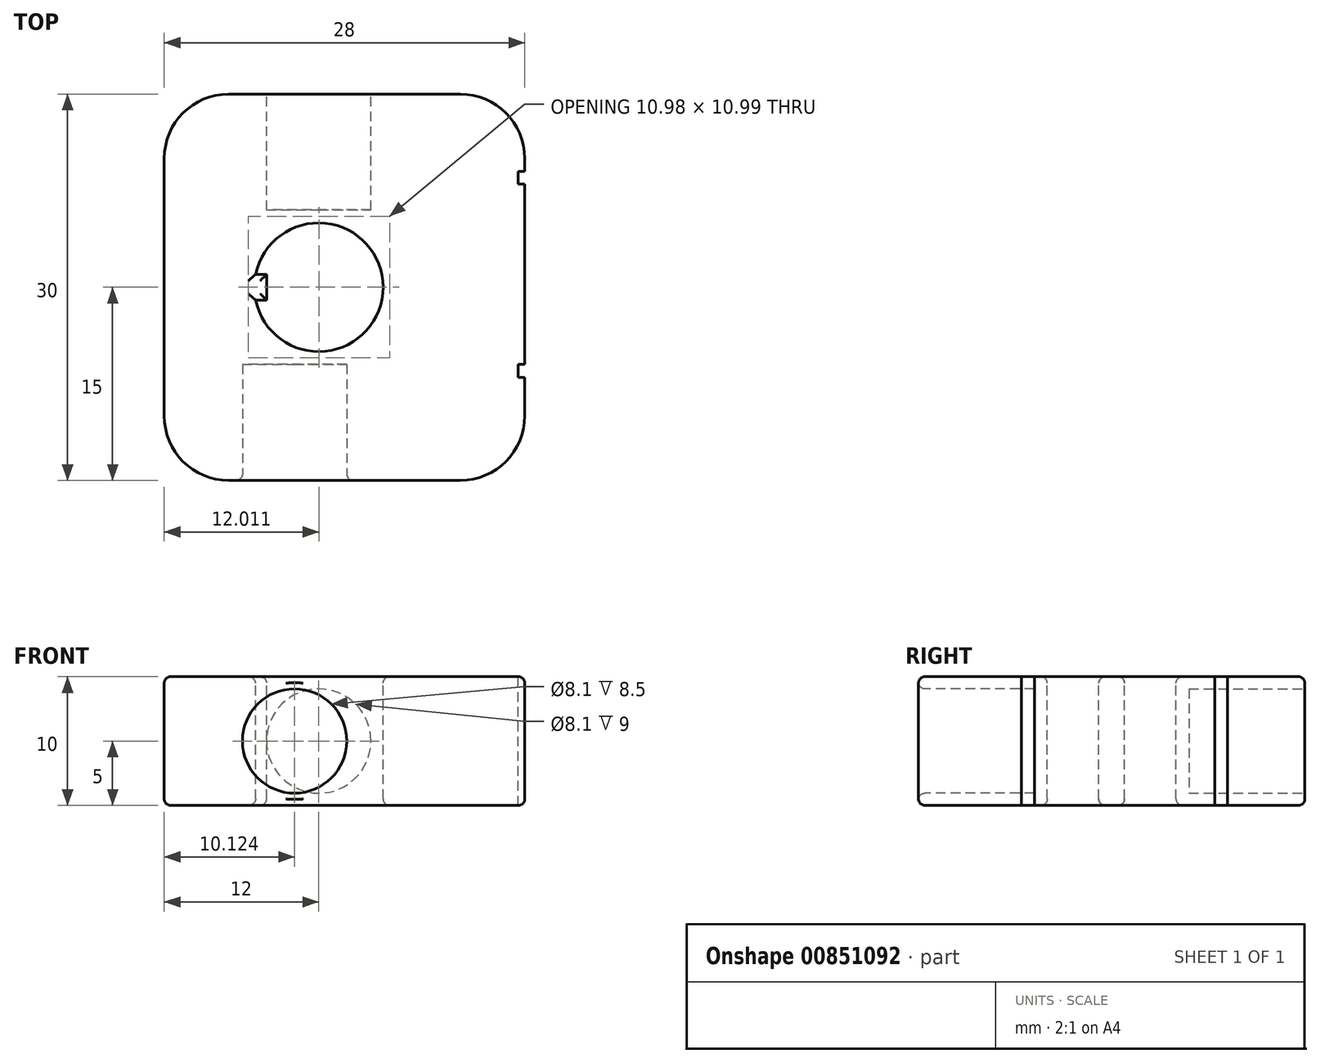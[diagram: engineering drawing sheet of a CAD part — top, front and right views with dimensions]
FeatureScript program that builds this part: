
annotation { "Feature Type Name" : "Feature", "Feature Type Description" : "" }
export const myFeature = defineFeature(function(context is Context, id is Id, definition is map)
    precondition{}
    {
        {
            var Q0;
            Q0=qCreatedBy(makeId("Top.planeOp"),FACE);
            var sketch = newSketch(context, id + "F0", { "sketchPlane" : qUnion([Q0])});
            skLineSegment(sketch, "E0.bottom", {"start": v(9, -15) * mm, "end": v(-9, -15) * mm});
            skLineSegment(sketch, "E0.top", {"start": v(9, 15) * mm, "end": v(-9, 15) * mm});
            skLineSegment(sketch, "E0.left", {"start": v(14, -10) * mm, "end": v(14, 10) * mm});
            skLineSegment(sketch, "E0.right", {"start": v(-14, -10) * mm, "end": v(-14, 10) * mm});
            skPoint(sketch, "E0.middle", {"position": v(0, 0) * mm});
            skPoint(sketch, "E1.visualSharp", {"position": v(-14, -15) * mm});
            skArc(sketch, "E1.filletArc", {"start": v(-14, -10) * mm, "mid": v(-12.54, -13.54) * mm, "end": v(-9, -15) * mm});
            skPoint(sketch, "E2.visualSharp", {"position": v(-14, 15) * mm});
            skArc(sketch, "E2.filletArc", {"start": v(-9, 15) * mm, "mid": v(-12.54, 13.54) * mm, "end": v(-14, 10) * mm});
            skPoint(sketch, "E3.visualSharp", {"position": v(14, 15) * mm});
            skArc(sketch, "E3.filletArc", {"start": v(14, 10) * mm, "mid": v(12.54, 13.54) * mm, "end": v(9, 15) * mm});
            skPoint(sketch, "E4.visualSharp", {"position": v(14, -15) * mm});
            skArc(sketch, "E4.filletArc", {"start": v(9, -15) * mm, "mid": v(12.54, -13.54) * mm, "end": v(14, -10) * mm});
            skSolve(sketch);
        }
        {
            var Q0;
            Q0=makeQuery(id+"F0.imprint","IMPRINT",FACE,{"disambiguationData":[TD([[makeQuery(id+"F0.imprint","IMPRINT",EDGE,{"derivedFrom":sQuery(id+"F0.wireOp",EDGE,"E0.bottom")}),-1.0]])]});
            extrude(context, id + "F1", {"entities" : qUnion([Q0]), "depth" : 10 * mm, "offsetDistance" : 25 * mm});
        }
        {
            var Q0;
            Q0=makeQuery(id+"F1.opExtrude","SWEPT_FACE",FACE,{"disambiguationData":[OSD([sQuery(id+"F0.wireOp",EDGE,"E0.bottom")])]});
            var sketch = newSketch(context, id + "F2", { "sketchPlane" : qUnion([Q0])});
            skCircle(sketch, "E5", {"center": v(-3.88, 5) * mm, "radius": 4.05 * mm});
            skSolve(sketch);
        }
        {
            var Q0;
            Q0 = qSketchRegion(id + "F2", true);
            extrude(context, id + "F3", {"entities" : qUnion([Q0]), "operationType" : NewBodyOperationType.REMOVE, "oppositeDirection" : true, "depth" : 9 * mm, "offsetDistance" : 25 * mm});
        }
        {
            var Q0;
            Q0=makeQuery(id+"F1.opExtrude","SWEPT_FACE",FACE,{"disambiguationData":[OSD([sQuery(id+"F0.wireOp",EDGE,"E0.top")])]});
            var sketch = newSketch(context, id + "F4", { "sketchPlane" : qUnion([Q0])});
            skCircle(sketch, "E6", {"center": v(2, 5) * mm, "radius": 4.05 * mm});
            skSolve(sketch);
        }
        {
            var Q0;
            Q0 = qSketchRegion(id + "F4", true);
            extrude(context, id + "F5", {"entities" : qUnion([Q0]), "operationType" : NewBodyOperationType.REMOVE, "oppositeDirection" : true, "depth" : 9 * mm, "offsetDistance" : 25 * mm});
        }
        {
            var Q0;
            Q0=makeQuery(id+"F1.opExtrude","CAP_FACE",FACE,{"disambiguationData":[OSD([sQuery(id+"F0.wireOp",EDGE,"E0.bottom"),sQuery(id+"F0.wireOp",EDGE,"E0.top"),sQuery(id+"F0.wireOp",EDGE,"E0.left"),sQuery(id+"F0.wireOp",EDGE,"E0.right"),sQuery(id+"F0.wireOp",EDGE,"E1.filletArc"),sQuery(id+"F0.wireOp",EDGE,"E2.filletArc"),sQuery(id+"F0.wireOp",EDGE,"E3.filletArc"),sQuery(id+"F0.wireOp",EDGE,"E4.filletArc")])],"isStart":false});
            var sketch = newSketch(context, id + "F6", { "sketchPlane" : qUnion([Q0])});
            skArc(sketch, "E7", {"start": v(-6.9, -1) * mm, "mid": v(3, 0) * mm, "end": v(-6.9, 1) * mm});
            skLineSegment(sketch, "E8.bottom", {"start": v(-6.9, 1) * mm, "end": v(-6.05, 1) * mm});
            skLineSegment(sketch, "E8.top", {"start": v(-6.9, -1) * mm, "end": v(-6.05, -1) * mm});
            skLineSegment(sketch, "E8.right", {"start": v(-6.05, 1) * mm, "end": v(-6.05, -1) * mm});
            skSolve(sketch);
        }
        {
            var Q0;
            Q0 = qSketchRegion(id + "F6", true);
            extrude(context, id + "F7", {"entities" : qUnion([Q0]), "operationType" : NewBodyOperationType.REMOVE, "endBound" : BoundingType.THROUGH_ALL, "oppositeDirection" : true, "depth" : 25 * mm, "offsetDistance" : 25 * mm});
        }
        {
            var Q0;
            Q0=makeQuery(id+"F1.opExtrude","CAP_FACE",FACE,{"disambiguationData":[OSD([sQuery(id+"F0.wireOp",EDGE,"E0.bottom"),sQuery(id+"F0.wireOp",EDGE,"E0.top"),sQuery(id+"F0.wireOp",EDGE,"E0.left"),sQuery(id+"F0.wireOp",EDGE,"E0.right"),sQuery(id+"F0.wireOp",EDGE,"E1.filletArc"),sQuery(id+"F0.wireOp",EDGE,"E2.filletArc"),sQuery(id+"F0.wireOp",EDGE,"E3.filletArc"),sQuery(id+"F0.wireOp",EDGE,"E4.filletArc")])],"isStart":false});
            var Q1;
            Q1=makeQuery(id+"F1.opExtrude","SWEPT_FACE",FACE,{"disambiguationData":[OSD([sQuery(id+"F0.wireOp",EDGE,"E0.bottom")])]});
            var Q2;
            Q2=makeQuery(id+"F1.opExtrude","CAP_FACE",FACE,{"disambiguationData":[OSD([sQuery(id+"F0.wireOp",EDGE,"E0.bottom"),sQuery(id+"F0.wireOp",EDGE,"E0.top"),sQuery(id+"F0.wireOp",EDGE,"E0.left"),sQuery(id+"F0.wireOp",EDGE,"E0.right"),sQuery(id+"F0.wireOp",EDGE,"E1.filletArc"),sQuery(id+"F0.wireOp",EDGE,"E2.filletArc"),sQuery(id+"F0.wireOp",EDGE,"E3.filletArc"),sQuery(id+"F0.wireOp",EDGE,"E4.filletArc")])],"isStart":true});
            fillet(context, id + "F8", {"entities" : qUnion([Q0, Q1, Q2]), "radius" : 0.5 * mm, "tangentPropagation" : true, "allowEdgeOverflow" : false});
        }
        {
            var Q0;
            Q0=makeQuery(id+"F1.opExtrude","CAP_FACE",FACE,{"disambiguationData":[OSD([sQuery(id+"F0.wireOp",EDGE,"E0.bottom"),sQuery(id+"F0.wireOp",EDGE,"E0.top"),sQuery(id+"F0.wireOp",EDGE,"E0.left"),sQuery(id+"F0.wireOp",EDGE,"E0.right"),sQuery(id+"F0.wireOp",EDGE,"E1.filletArc"),sQuery(id+"F0.wireOp",EDGE,"E2.filletArc"),sQuery(id+"F0.wireOp",EDGE,"E3.filletArc"),sQuery(id+"F0.wireOp",EDGE,"E4.filletArc")])],"isStart":false});
            var sketch = newSketch(context, id + "F9", { "sketchPlane" : qUnion([Q0])});
            skLineSegment(sketch, "E9.bottom", {"start": v(13.5, -6) * mm, "end": v(15.5, -6) * mm});
            skLineSegment(sketch, "E9.top", {"start": v(13.5, -7) * mm, "end": v(15.5, -7) * mm});
            skLineSegment(sketch, "E9.left", {"start": v(13.5, -6) * mm, "end": v(13.5, -7) * mm});
            skLineSegment(sketch, "E9.right", {"start": v(15.5, -6) * mm, "end": v(15.5, -7) * mm});
            skLineSegment(sketch, "E10.bottom", {"start": v(13.5, 9) * mm, "end": v(15.5, 9) * mm});
            skLineSegment(sketch, "E10.top", {"start": v(13.5, 8) * mm, "end": v(15.5, 8) * mm});
            skLineSegment(sketch, "E10.left", {"start": v(13.5, 9) * mm, "end": v(13.5, 8) * mm});
            skLineSegment(sketch, "E10.right", {"start": v(15.5, 9) * mm, "end": v(15.5, 8) * mm});
            skSolve(sketch);
        }
        {
            var Q0;
            Q0 = qSketchRegion(id + "F9", true);
            extrude(context, id + "F10", {"entities" : qUnion([Q0]), "operationType" : NewBodyOperationType.REMOVE, "endBound" : BoundingType.THROUGH_ALL, "oppositeDirection" : true, "depth" : 25 * mm, "offsetDistance" : 25 * mm});
        }
    });
